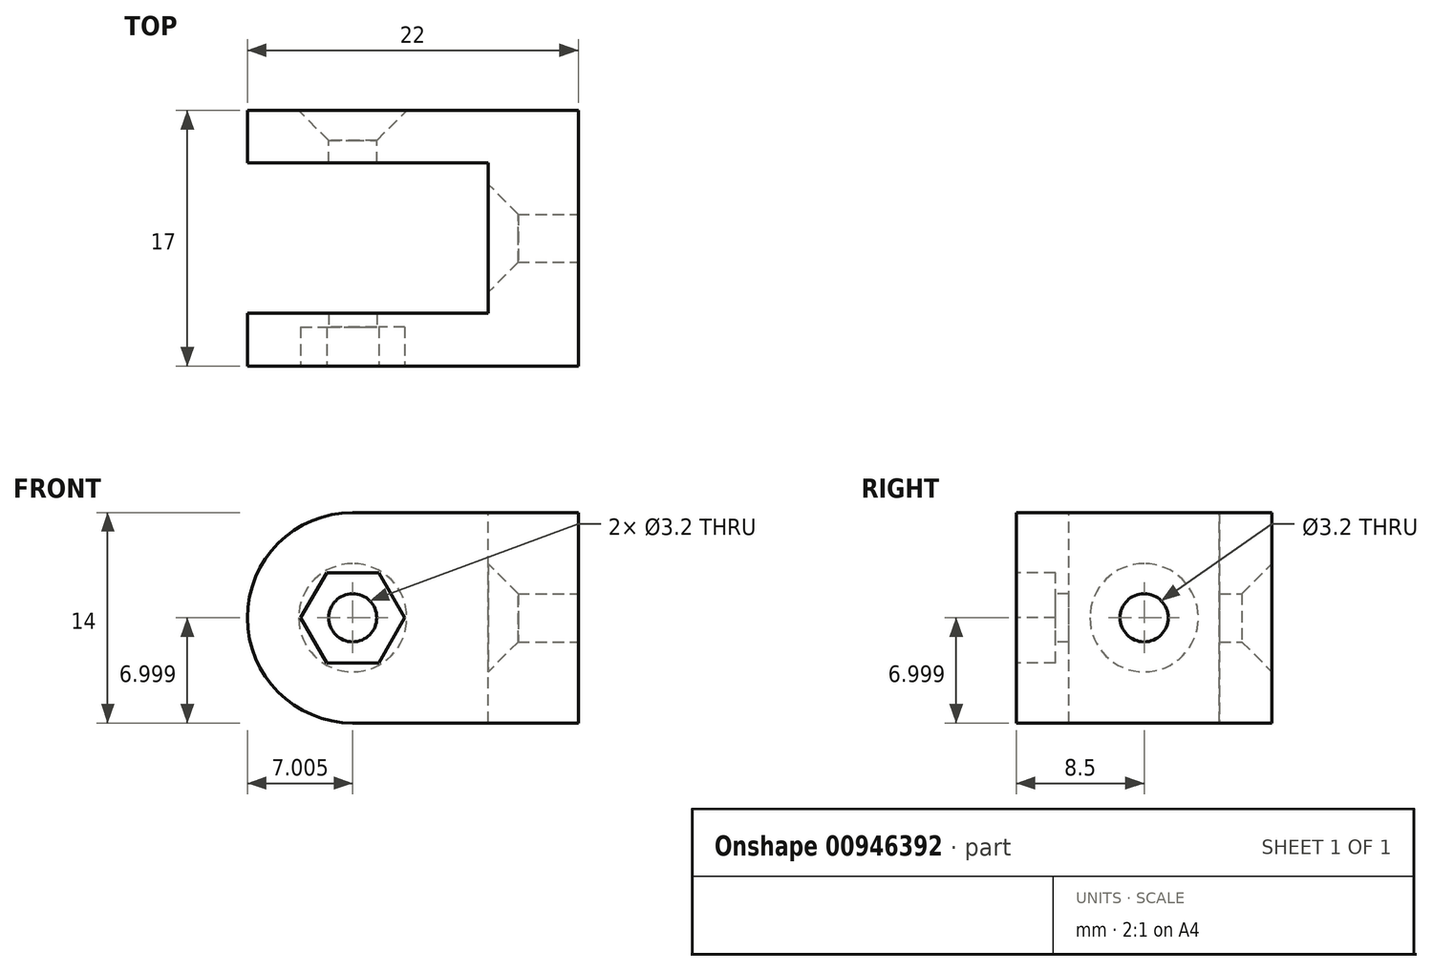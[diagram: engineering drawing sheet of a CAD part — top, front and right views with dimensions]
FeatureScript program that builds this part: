
annotation { "Feature Type Name" : "Feature", "Feature Type Description" : "" }
export const myFeature = defineFeature(function(context is Context, id is Id, definition is map)
    precondition{}
    {
        {
            var Q0;
            Q0=qCreatedBy(makeId("Front.planeOp"),FACE);
            var sketch = newSketch(context, id + "F0", { "sketchPlane" : qUnion([Q0])});
            skLineSegment(sketch, "E0", {"start": v(-44.06, 14.35) * mm, "end": v(-29.06, 14.35) * mm});
            skLineSegment(sketch, "E1", {"start": v(-29.06, 14.35) * mm, "end": v(-29.06, 0.35) * mm});
            skLineSegment(sketch, "E2", {"start": v(-29.06, 0.35) * mm, "end": v(-44.06, 0.35) * mm});
            skLineSegment(sketch, "E3", {"start": v(-44.06, 14.35) * mm, "end": v(-44.06, 0.35) * mm, "construction": true});
            skArc(sketch, "E4", {"start": v(-44.06, 14.35) * mm, "mid": v(-51.06, 7.35) * mm, "end": v(-44.06, 0.35) * mm});
            skLineSegment(sketch, "E5", {"start": v(-35.06, 14.35) * mm, "end": v(-35.06, 0.35) * mm, "construction": true});
            skLineSegment(sketch, "E6", {"start": v(-30.82, 7.35) * mm, "end": v(-46.88, 7.35) * mm, "construction": true});
            skCircle(sketch, "E7", {"center": v(-44.06, 7.35) * mm, "radius": 1.6 * mm});
            skLineSegment(sketch, "E8", {"start": v(-51.06, 18.1) * mm, "end": v(-51.06, -2.32) * mm, "construction": true});
            skSolve(sketch);
        }
        {
            var Q0;
            Q0=sQuery(id+"F0.wireOp",EDGE,"E2");
            cPoint(context, id + "F1", {"entities" : qUnion([Q0]), "parameter" : 0.5});
        }
        {
            var Q0;
            Q0=sQuery(id+"F0.wireOp",EDGE,"E1");
            var Q1;
            Q1 = qCreatedBy(id + "F1" ,VERTEX);
            cPlane(context, id + "F2", {"entities" : qUnion([Q0, Q1]), "cplaneType" : CPlaneType.LINE_ANGLE, "offset" : 25 * mm, "angle" : 90 * degree, "width" : 150 * mm, "height" : 150 * mm});
        }
        {
            var Q0;
            Q0=qCreatedBy(id+"F2.planeOp",FACE);
            var sketch = newSketch(context, id + "F3", { "sketchPlane" : qUnion([Q0])});
            skLineSegment(sketch, "E9.bottom", {"start": v(17, 14.35) * mm, "end": v(0, 14.35) * mm});
            skLineSegment(sketch, "E9.top", {"start": v(17, 0.35) * mm, "end": v(0, 0.35) * mm});
            skLineSegment(sketch, "E9.left", {"start": v(17, 14.35) * mm, "end": v(17, 0.35) * mm});
            skLineSegment(sketch, "E9.right", {"start": v(0, 14.35) * mm, "end": v(0, 0.35) * mm});
            skLineSegment(sketch, "E10", {"start": v(3.5, 14.35) * mm, "end": v(3.5, 0.35) * mm, "construction": true});
            skLineSegment(sketch, "E11", {"start": v(8.5, 48.47) * mm, "end": v(8.5, -37.47) * mm, "construction": true});
            skCircle(sketch, "E12", {"center": v(8.5, 7.35) * mm, "radius": 1.6 * mm});
            skPoint(sketch, "E12.centerSnap0", {"position": v(17, 7.35) * mm});
            skLineSegment(sketch, "E13.MirrorCS", {"start": v(13.5, 14.35) * mm, "end": v(13.5, 0.35) * mm, "construction": true});
            skSolve(sketch);
        }
        {
            var Q0;
            Q0=makeQuery(id+"F0.imprint","IMPRINT",FACE,{"disambiguationData":[TD([[makeQuery(id+"F0.imprint","IMPRINT",EDGE,{"derivedFrom":sQuery(id+"F0.wireOp",EDGE,"E0")}),-1.0]])]});
            var Q1;
            Q1=sQuery(id+"F3.wireOp",VERTEX,"E10.end");
            extrude(context, id + "F4", {"entities" : qUnion([Q0]), "endBound" : BoundingType.UP_TO_VERTEX, "oppositeDirection" : true, "depth" : 25 * mm, "endBoundEntityVertex" : qUnion([Q1]), "offsetDistance" : 25 * mm});
        }
        {
            var Q0;
            Q0=sQuery(id+"F3.wireOp",EDGE,"E11");
            cPlane(context, id + "F5", {"entities" : qUnion([Q0]), "cplaneType" : CPlaneType.LINE_ANGLE, "offset" : 25 * mm, "angle" : 90 * degree, "width" : 150 * mm, "height" : 150 * mm});
        }
        {
            var Q0;
            Q0=makeQuery(id+"F4.opExtrude","SWEPT_BODY",BODY,{"disambiguationData":[OSD([sQuery(id+"F0.wireOp",EDGE,"E0"),sQuery(id+"F0.wireOp",EDGE,"E1"),sQuery(id+"F0.wireOp",EDGE,"E2"),sQuery(id+"F0.wireOp",EDGE,"E4"),sQuery(id+"F0.wireOp",EDGE,"E7")])]});
            var Q1;
            Q1=qCreatedBy(id+"F5.planeOp",FACE);
            mirror(context, id + "F6", {"operationType" : NewBodyOperationType.ADD, "entities" : qUnion([Q0]), "mirrorPlane" : qUnion([Q1])});
        }
        {
            var Q0;
            Q0=makeQuery(id+"F3.imprint","IMPRINT",FACE,{"disambiguationData":[TD([[makeQuery(id+"F3.imprint","IMPRINT",EDGE,{"derivedFrom":sQuery(id+"F3.wireOp",EDGE,"E9.bottom")}),1.0]])]});
            var Q1;
            Q1=sQuery(id+"F0.wireOp",VERTEX,"E5.end");
            extrude(context, id + "F7", {"entities" : qUnion([Q0]), "operationType" : NewBodyOperationType.ADD, "endBound" : BoundingType.UP_TO_VERTEX, "oppositeDirection" : true, "depth" : 25 * mm, "endBoundEntityVertex" : qUnion([Q1]), "offsetDistance" : 25 * mm});
        }
        {
            var Q0;
            Q0=makeQuery(id+"F0.imprint","IMPRINT",FACE,{"disambiguationData":[TD([[makeQuery(id+"F0.imprint","IMPRINT",EDGE,{"derivedFrom":sQuery(id+"F0.wireOp",EDGE,"E0")}),-1.0]])]});
            var sketch = newSketch(context, id + "F8", { "sketchPlane" : qUnion([Q0])});
            skCircle(sketch, "E14.cCircle", {"center": v(-44.06, 7.35) * mm, "radius": 3 * mm, "construction": true});
            skLineSegment(sketch, "E14.0", {"start": v(-45.79, 10.35) * mm, "end": v(-42.32, 10.35) * mm});
            skLineSegment(sketch, "E14.1", {"start": v(-42.32, 10.35) * mm, "end": v(-40.6, 7.35) * mm});
            skLineSegment(sketch, "E14.2", {"start": v(-40.6, 7.35) * mm, "end": v(-42.32, 4.35) * mm});
            skLineSegment(sketch, "E14.3", {"start": v(-42.32, 4.35) * mm, "end": v(-45.79, 4.35) * mm});
            skLineSegment(sketch, "E14.4", {"start": v(-45.79, 4.35) * mm, "end": v(-47.52, 7.35) * mm});
            skLineSegment(sketch, "E14.5", {"start": v(-47.52, 7.35) * mm, "end": v(-45.79, 10.35) * mm});
            skPoint(sketch, "E14.0.midPoint", {"position": v(-44.06, 10.35) * mm});
            skSolve(sketch);
        }
        {
            var Q0;
            Q0=makeQuery(id+"F8.imprint","IMPRINT",FACE,{"disambiguationData":[TD([[makeQuery(id+"F8.imprint","IMPRINT",EDGE,{"derivedFrom":sQuery(id+"F8.wireOp",EDGE,"E14.0")}),-1.0]])]});
            extrude(context, id + "F9", {"entities" : qUnion([Q0]), "operationType" : NewBodyOperationType.REMOVE, "oppositeDirection" : true, "depth" : 2.6 * mm, "offsetDistance" : 25 * mm});
        }
        {
            var Q0;
            Q0=makeQuery(id+"F6.opPattern","COPY",EDGE,{"derivedFrom":makeQuery(id+"F4.opExtrude","CAP_EDGE",EDGE,{"disambiguationData":[OSD([sQuery(id+"F0.wireOp",EDGE,"E7")])],"isStart":true}),"instanceName":"1"});
            var Q1;
            Q1=makeQuery(id+"F7.opExtrude","CAP_EDGE",EDGE,{"disambiguationData":[OSD([sQuery(id+"F3.wireOp",EDGE,"E12")])],"isStart":false});
            chamfer(context, id + "F10", {"entities" : qUnion([Q0, Q1]), "width" : 2 * mm, "tangentPropagation" : true});
        }
    });
